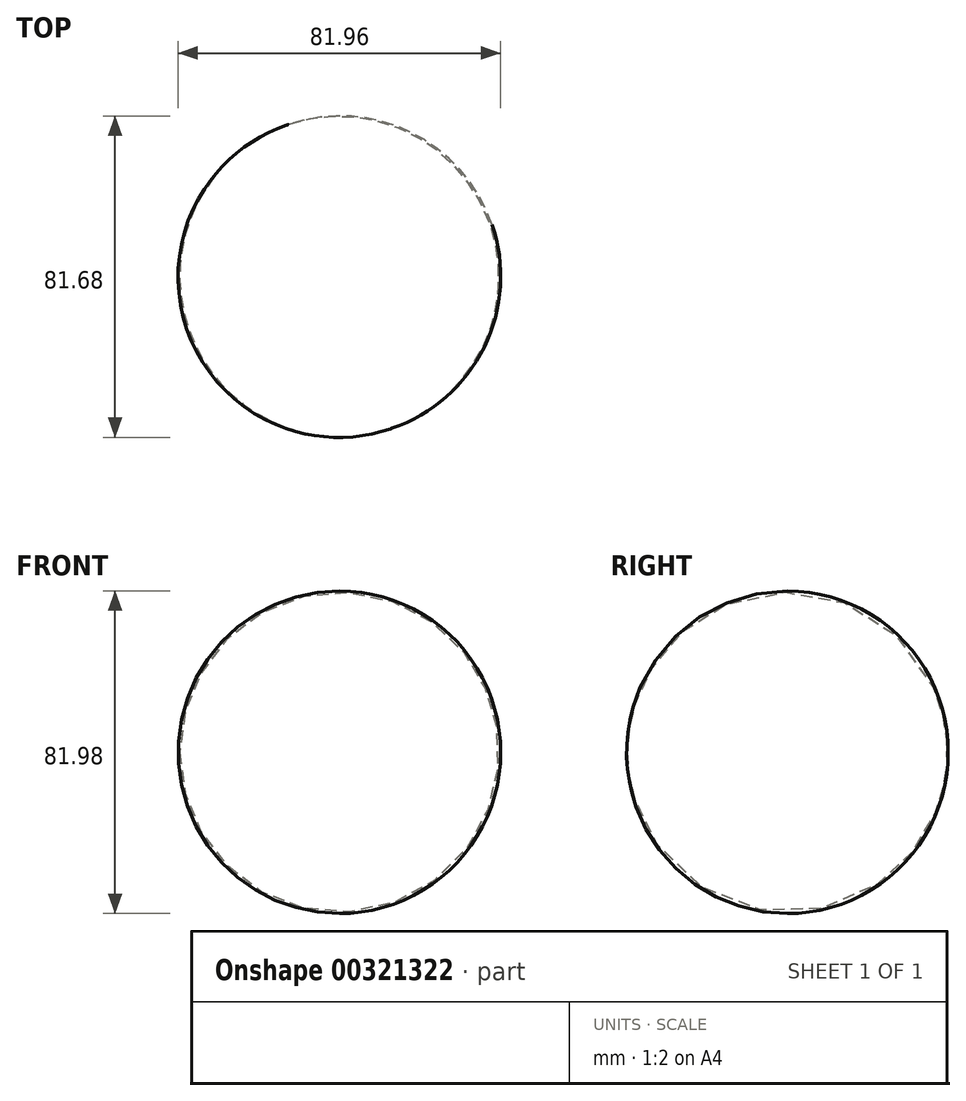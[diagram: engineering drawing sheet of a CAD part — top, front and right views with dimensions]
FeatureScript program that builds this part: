
annotation { "Feature Type Name" : "Feature", "Feature Type Description" : "" }
export const myFeature = defineFeature(function(context is Context, id is Id, definition is map)
    precondition{}
    {
        {
            var Q0;
            Q0=qCreatedBy(makeId("Top.planeOp"),FACE);
            var sketch = newSketch(context, id + "F0", { "sketchPlane" : qUnion([Q0])});
            skArc(sketch, "E0", {"start": v(-13.4, 38.5) * mm, "mid": v(-38.58, -13.18) * mm, "end": v(12.97, -38.65) * mm});
            skLineSegment(sketch, "E1", {"start": v(-13.4, 38.5) * mm, "end": v(12.97, -38.65) * mm, "construction": true});
            skSolve(sketch);
        }
        {
            var Q0;
            Q0=sQuery(id+"F0.wireOp",EDGE,"E0");
            var Q1;
            Q1=sQuery(id+"F0.wireOp",EDGE,"E1");
            revolve(context, id + "F1", {"bodyType" : ToolBodyType.SURFACE, "operationType" : NewBodyOperationType.ADD, "surfaceEntities" : qUnion([Q0]), "axis" : qUnion([Q1]), "revolveType" : RevolveType.FULL});
        }
    });
